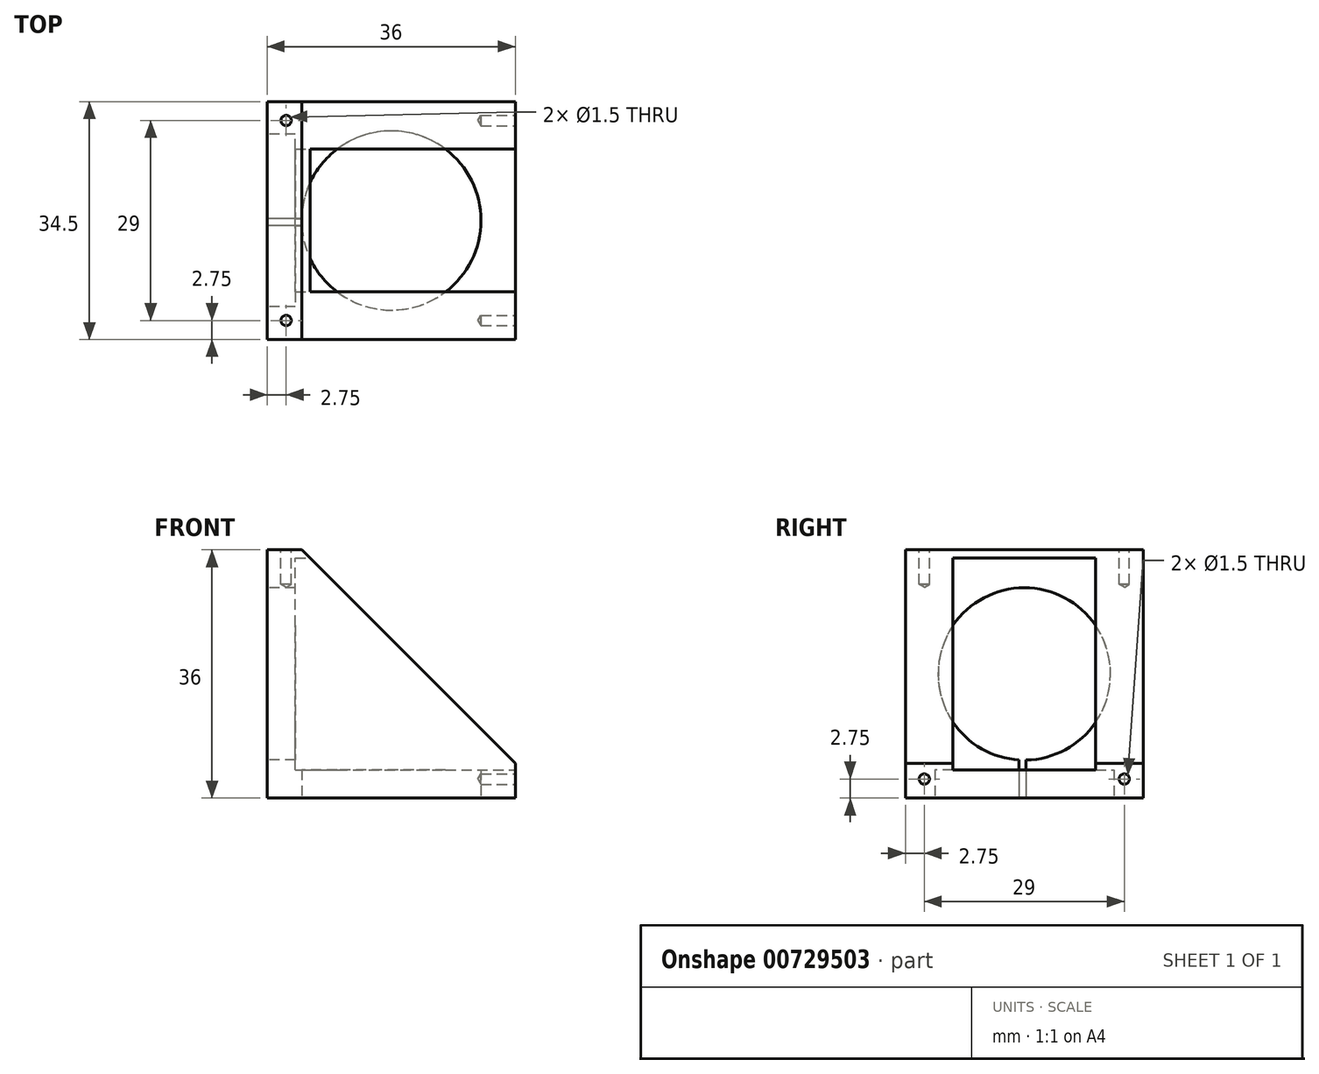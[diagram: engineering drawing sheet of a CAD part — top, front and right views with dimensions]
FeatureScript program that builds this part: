
annotation { "Feature Type Name" : "Feature", "Feature Type Description" : "" }
export const myFeature = defineFeature(function(context is Context, id is Id, definition is map)
    precondition{}
    {
        {
            var Q0;
            Q0=qCreatedBy(makeId("Front.planeOp"),FACE);
            var sketch = newSketch(context, id + "F0", { "sketchPlane" : qUnion([Q0])});
            skLineSegment(sketch, "E0", {"start": v(0, 0) * mm, "end": v(36, 0) * mm});
            skLineSegment(sketch, "E1", {"start": v(36, 0) * mm, "end": v(36, 5) * mm});
            skLineSegment(sketch, "E2", {"start": v(36, 5) * mm, "end": v(5, 36) * mm});
            skLineSegment(sketch, "E3", {"start": v(5, 36) * mm, "end": v(0, 36) * mm});
            skLineSegment(sketch, "E4", {"start": v(0, 36) * mm, "end": v(0, 0) * mm});
            skSolve(sketch);
        }
        {
            var Q0;
            Q0=makeQuery(id+"F0.imprint","IMPRINT",FACE,{"disambiguationData":[TD([[makeQuery(id+"F0.imprint","IMPRINT",EDGE,{"derivedFrom":sQuery(id+"F0.wireOp",EDGE,"E0")}),1.0]])]});
            extrude(context, id + "F1", {"entities" : qUnion([Q0]), "depth" : 34.5 * mm, "offsetDistance" : 25 * mm});
        }
        {
            var Q0;
            Q0=makeQuery(id+"F1.opExtrude","SWEPT_FACE",FACE,{"disambiguationData":[OSD([sQuery(id+"F0.wireOp",EDGE,"E4")])]});
            var sketch = newSketch(context, id + "F2", { "sketchPlane" : qUnion([Q0])});
            skCircle(sketch, "E5", {"center": v(17.25, 18) * mm, "radius": 12.5 * mm});
            skSolve(sketch);
        }
        {
            var Q0;
            Q0=makeQuery(id+"F2.imprint","IMPRINT",FACE,{"disambiguationData":[TD([[makeQuery(id+"F2.imprint","IMPRINT",EDGE,{"derivedFrom":sQuery(id+"F2.wireOp",EDGE,"E5")}),1.0]])]});
            extrude(context, id + "F3", {"entities" : qUnion([Q0]), "operationType" : NewBodyOperationType.REMOVE, "oppositeDirection" : true, "depth" : 4.1 * mm, "offsetDistance" : 25 * mm});
        }
        {
            var Q0;
            Q0=makeQuery(id+"F1.opExtrude","SWEPT_FACE",FACE,{"disambiguationData":[OSD([sQuery(id+"F0.wireOp",EDGE,"E0")])]});
            var sketch = newSketch(context, id + "F4", { "sketchPlane" : qUnion([Q0])});
            skCircle(sketch, "E6", {"center": v(18, 17.25) * mm, "radius": 13 * mm});
            skSolve(sketch);
        }
        {
            var Q0;
            Q0=makeQuery(id+"F4.imprint","IMPRINT",FACE,{"disambiguationData":[TD([[makeQuery(id+"F4.imprint","IMPRINT",EDGE,{"derivedFrom":sQuery(id+"F4.wireOp",EDGE,"E6")}),1.0]])]});
            extrude(context, id + "F5", {"entities" : qUnion([Q0]), "operationType" : NewBodyOperationType.REMOVE, "oppositeDirection" : true, "depth" : 4.1 * mm, "offsetDistance" : 25 * mm});
        }
        {
            var Q0;
            Q0=makeQuery(id+"F1.opExtrude","SWEPT_FACE",FACE,{"disambiguationData":[OSD([sQuery(id+"F0.wireOp",EDGE,"E1")])]});
            var sketch = newSketch(context, id + "F6", { "sketchPlane" : qUnion([Q0])});
            skLineSegment(sketch, "E7.bottom", {"start": v(-27.6, 4.1) * mm, "end": v(-6.9, 4.1) * mm});
            skLineSegment(sketch, "E7.top", {"start": v(-27.6, 34.8) * mm, "end": v(-6.9, 34.8) * mm});
            skLineSegment(sketch, "E7.left", {"start": v(-27.6, 4.1) * mm, "end": v(-27.6, 34.8) * mm});
            skLineSegment(sketch, "E7.right", {"start": v(-6.9, 4.1) * mm, "end": v(-6.9, 34.8) * mm});
            skSolve(sketch);
        }
        {
            var Q0;
            {var subQ0=sQuery(id+"F6.wireOp",EDGE,"E7.top");Q0=makeQuery(id+"F6.imprint","IMPRINT",FACE,{"disambiguationData":[TD([[makeQuery(id+"F6.imprint","IMPRINT",EDGE,{"derivedFrom":subQ0}),-1.0]])]});}
            var Q1;
            {var subQ0=sQuery(id+"F6.wireOp",EDGE,"E7.bottom");Q1=makeQuery(id+"F6.imprint","IMPRINT",FACE,{"disambiguationData":[TD([[makeQuery(id+"F6.imprint","IMPRINT",EDGE,{"derivedFrom":subQ0}),1.0]])]});}
            extrude(context, id + "F7", {"entities" : qUnion([Q0, Q1]), "operationType" : NewBodyOperationType.REMOVE, "oppositeDirection" : true, "depth" : (36 - 4.1) * mm, "offsetDistance" : 25 * mm});
        }
        {
            var Q0;
            Q0=makeQuery(id+"F1.opExtrude","SWEPT_FACE",FACE,{"disambiguationData":[OSD([sQuery(id+"F0.wireOp",EDGE,"E3")])]});
            var sketch = newSketch(context, id + "F8", { "sketchPlane" : qUnion([Q0])});
            skPoint(sketch, "E8", {"position": v(2.75, -2.75) * mm});
            skPoint(sketch, "E9", {"position": v(2.75, -31.75) * mm});
            skSolve(sketch);
        }
        {
            var Q0;
            Q0=makeQuery(id+"F1.opExtrude","SWEPT_FACE",FACE,{"disambiguationData":[OSD([sQuery(id+"F0.wireOp",EDGE,"E1")])]});
            var sketch = newSketch(context, id + "F9", { "sketchPlane" : qUnion([Q0])});
            skPoint(sketch, "E10", {"position": v(-31.75, 2.75) * mm});
            skPoint(sketch, "E11", {"position": v(-2.75, 2.75) * mm});
            skSolve(sketch);
        }
        {
            var Q0;
            Q0=sQuery(id+"F8.wireOp",VERTEX,"E9");
            var Q1;
            Q1=sQuery(id+"F8.wireOp",VERTEX,"E8");
            var Q2;
            Q2=sQuery(id+"F9.wireOp",VERTEX,"E10");
            var Q3;
            Q3=sQuery(id+"F9.wireOp",VERTEX,"E11");
            var Q4;
            Q4=makeQuery(id+"F1.opExtrude","SWEPT_BODY",BODY,{"disambiguationData":[OSD([sQuery(id+"F0.wireOp",EDGE,"E0"),sQuery(id+"F0.wireOp",EDGE,"E1"),sQuery(id+"F0.wireOp",EDGE,"E2"),sQuery(id+"F0.wireOp",EDGE,"E3"),sQuery(id+"F0.wireOp",EDGE,"E4")])]});
            hole(context, id + "F10", {"style" : HoleStyle.SIMPLE, "endStyle" : HoleEndStyle.BLIND, "holeDiameter" : 1.5 * mm, "majorDiameter" : 5 * mm, "holeDepth" : 5 * mm, "isTappedThrough" : true, "tappedDepth" : 12 * mm, "tapClearance" : 3, "startFromSketch" : true, "locations" : qUnion([Q0, Q1, Q2, Q3]), "scope" : qUnion([Q4])});
        }
        {
            var Q0;
            Q0=makeQuery(id+"F1.opExtrude","SWEPT_FACE",FACE,{"disambiguationData":[OSD([sQuery(id+"F0.wireOp",EDGE,"E4")])]});
            var sketch = newSketch(context, id + "F11", { "sketchPlane" : qUnion([Q0])});
            skLineSegment(sketch, "E12.bottom", {"start": v(17, 10) * mm, "end": v(18, 10) * mm});
            skLineSegment(sketch, "E12.top", {"start": v(17, 0) * mm, "end": v(18, 0) * mm});
            skLineSegment(sketch, "E12.left", {"start": v(17, 10) * mm, "end": v(17, 0) * mm});
            skLineSegment(sketch, "E12.right", {"start": v(18, 10) * mm, "end": v(18, 0) * mm});
            skSolve(sketch);
        }
        {
            var Q0;
            {var subQ0=sQuery(id+"F11.wireOp",EDGE,"E12.top");Q0=makeQuery(id+"F11.imprint","IMPRINT",FACE,{"disambiguationData":[TD([[makeQuery(id+"F11.imprint","IMPRINT",EDGE,{"derivedFrom":subQ0}),-1.0]])]});}
            extrude(context, id + "F12", {"entities" : qUnion([Q0]), "operationType" : NewBodyOperationType.REMOVE, "oppositeDirection" : true, "depth" : 25 * mm, "offsetDistance" : 25 * mm});
        }
    });
